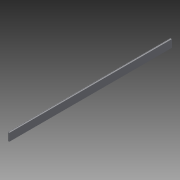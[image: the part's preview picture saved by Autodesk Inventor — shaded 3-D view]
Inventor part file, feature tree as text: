
AUTODESK INVENTOR PART (.ipt)
format: ipt  version: 2015 SP1 (Build 190203100, 203)  size: 79,872 bytes
history: native  units: in
note: dims shown in document units (in); Inventor stores cm internally (conversion verified against a paired STEP export)
features: extrude x1, sketch x1
ambient origin geometry x8: Origin, YZ Plane, XZ Plane, XY Plane, X Axis, Y Axis, Z Axis, Center Point
bodies: Solid1 (feature_tree)
feature tree (2):
  extrude  "Extrusion1"  Depth=0.6299in
  sketch  "Sketch1"  dims[d0=3.937in d1=0.6299in d2=78.7402in d3=0.0in d4=0.1181in d5=0.1181in d6=0.0787in d7=0.2362in]
